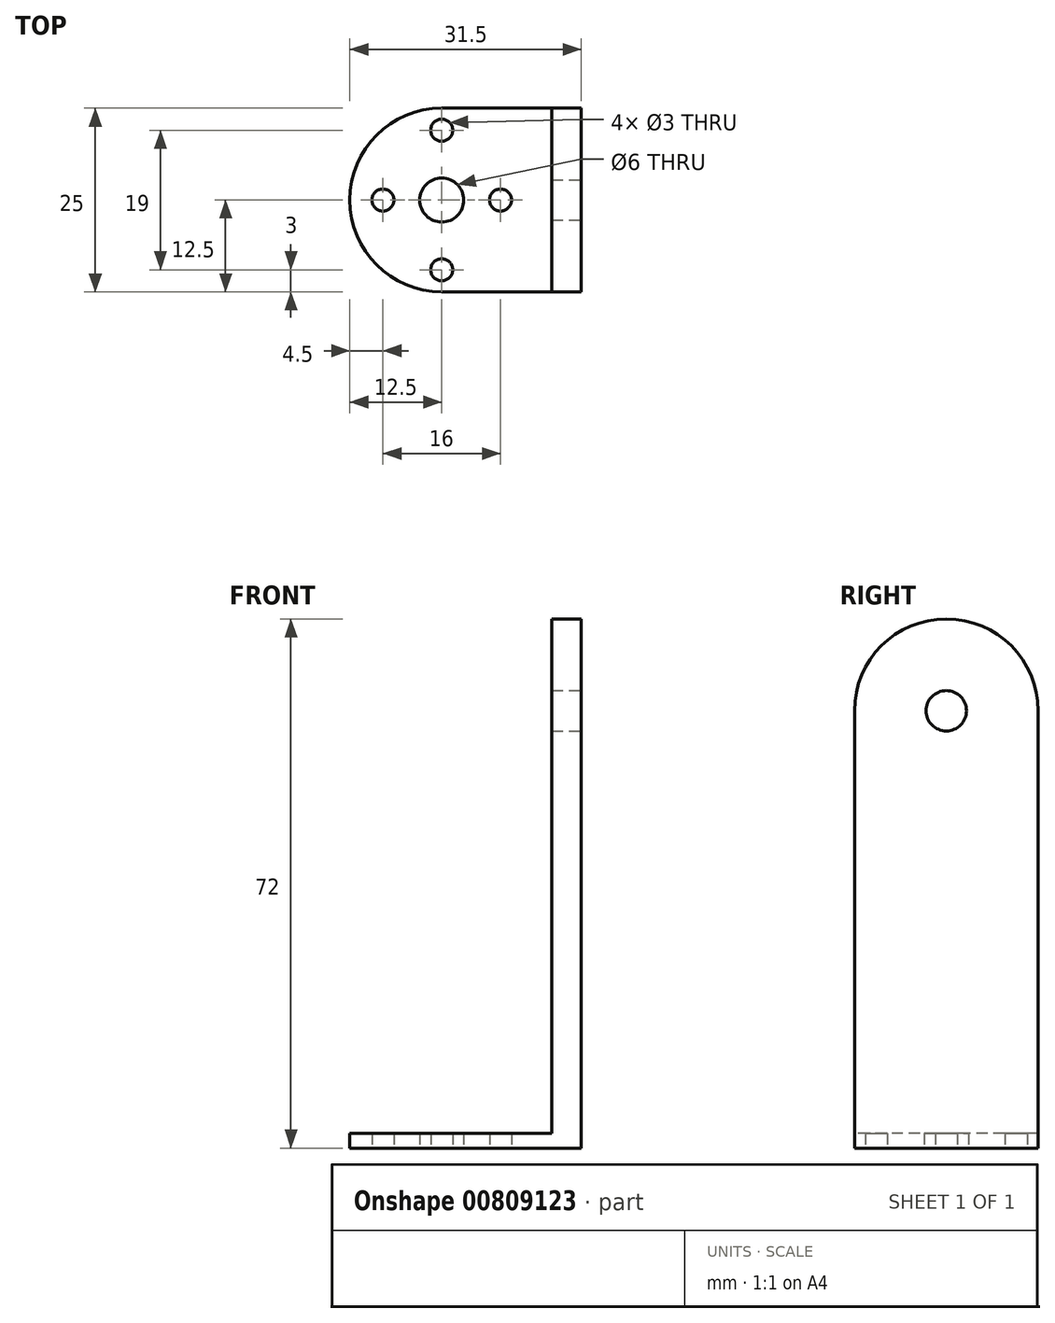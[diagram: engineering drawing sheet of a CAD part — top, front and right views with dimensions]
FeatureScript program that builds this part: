
annotation { "Feature Type Name" : "Feature", "Feature Type Description" : "" }
export const myFeature = defineFeature(function(context is Context, id is Id, definition is map)
    precondition{}
    {
        {
            var Q0;
            Q0=qCreatedBy(makeId("Top.planeOp"),FACE);
            var sketch = newSketch(context, id + "F0", { "sketchPlane" : qUnion([Q0])});
            skPoint(sketch, "E0.middle", {"position": v(0, 0) * mm});
            skCircle(sketch, "E1", {"center": v(0, 0) * mm, "radius": 9.5 * mm});
            skCircle(sketch, "E2", {"center": v(0, 0) * mm, "radius": 8 * mm});
            skCircle(sketch, "E3", {"center": v(0, -9.5) * mm, "radius": 1.5 * mm});
            skCircle(sketch, "E4", {"center": v(-8, 0) * mm, "radius": 1.5 * mm});
            skCircle(sketch, "E5", {"center": v(8, 0) * mm, "radius": 1.5 * mm});
            skCircle(sketch, "E6", {"center": v(0, 0) * mm, "radius": 12.5 * mm});
            skCircle(sketch, "E7", {"center": v(0, 0) * mm, "radius": 3 * mm});
            skCircle(sketch, "E8", {"center": v(0, 9.5) * mm, "radius": 1.5 * mm});
            skLineSegment(sketch, "E9", {"start": v(0, 12.5) * mm, "end": v(19, 12.5) * mm});
            skLineSegment(sketch, "E10", {"start": v(19, 12.5) * mm, "end": v(19, -12.5) * mm});
            skLineSegment(sketch, "E11", {"start": v(19, -12.5) * mm, "end": v(0, -12.5) * mm});
            skSolve(sketch);
        }
        {
            var Q0;
            Q0=makeQuery(id+"F0.imprint","IMPRINT",FACE,{"disambiguationData":[TD([[makeQuery(id+"F0.imprint","IMPRINT",EDGE,{"derivedFrom":sQuery(id+"F0.wireOp",EDGE,"E6")}),1.0]])]});
            var Q1;
            {var subQ0=sQuery(id+"F0.wireOp",EDGE,"PB5VHjtn-gHTu-7EB1-5jxL-tvkM96rimPre");var subQ1=sQuery(id+"F0.wireOp",EDGE,"E1");var subQ2=makeQuery(id+"F0.imprint","INTERSECT",VERTEX,{"disambiguationData":[OD(0.0)],"derivedFrom":[subQ1,subQ0]});Q1=makeQuery(id+"F0.imprint","IMPRINT",FACE,{"disambiguationData":[TD([[makeQuery(id+"F0.imprint","IMPRINT",EDGE,{"disambiguationData":[TD([[subQ2,1.0]])],"derivedFrom":subQ1}),1.0]])]});}
            var Q2;
            {var subQ0=sQuery(id+"F0.wireOp",EDGE,"PB5VHjtn-gHTu-7EB1-5jxL-tvkM96rimPre");var subQ1=sQuery(id+"F0.wireOp",EDGE,"E1");var subQ2=makeQuery(id+"F0.imprint","INTERSECT",VERTEX,{"disambiguationData":[OD(1.0)],"derivedFrom":[subQ1,subQ0]});Q2=makeQuery(id+"F0.imprint","IMPRINT",FACE,{"disambiguationData":[TD([[makeQuery(id+"F0.imprint","IMPRINT",EDGE,{"disambiguationData":[TD([[subQ2,-1.0]])],"derivedFrom":subQ1}),1.0]])]});}
            var Q3;
            {var subQ0=sQuery(id+"F0.wireOp",EDGE,"E4");var subQ1=sQuery(id+"F0.wireOp",EDGE,"E1");var subQ2=makeQuery(id+"F0.imprint","INTERSECT",VERTEX,{"derivedFrom":[subQ1,subQ0]});Q3=makeQuery(id+"F0.imprint","IMPRINT",FACE,{"disambiguationData":[TD([[makeQuery(id+"F0.imprint","IMPRINT",EDGE,{"disambiguationData":[TD([[subQ2,-1.0]])],"derivedFrom":subQ1}),1.0]])]});}
            var Q4;
            {var subQ0=sQuery(id+"F0.wireOp",EDGE,"E5");var subQ1=sQuery(id+"F0.wireOp",EDGE,"E1");var subQ2=makeQuery(id+"F0.imprint","INTERSECT",VERTEX,{"derivedFrom":[subQ1,subQ0]});Q4=makeQuery(id+"F0.imprint","IMPRINT",FACE,{"disambiguationData":[TD([[makeQuery(id+"F0.imprint","IMPRINT",EDGE,{"disambiguationData":[TD([[subQ2,1.0]])],"derivedFrom":subQ1}),1.0]])]});}
            var Q5;
            {var subQ0=sQuery(id+"F0.wireOp",EDGE,"E2");var subQ7=makeQuery(id+"F0.imprint","INTERSECT",VERTEX,{"derivedFrom":[subQ0,sQuery(id+"F0.wireOp",EDGE,"PB5VHjtn-gHTu-7EB1-5jxL-tvkM96rimPre")]});Q5=makeQuery(id+"F0.imprint","IMPRINT",FACE,{"disambiguationData":[TD([[makeQuery(id+"F0.imprint","IMPRINT",EDGE,{"disambiguationData":[TD([[subQ7,1.0]])],"derivedFrom":subQ0}),1.0]])]});}
            var Q6;
            {var subQ0=sQuery(id+"F0.wireOp",EDGE,"E8");var subQ1=sQuery(id+"F0.wireOp",EDGE,"E1");var subQ2=makeQuery(id+"F0.imprint","INTERSECT",VERTEX,{"disambiguationData":[OD(1.0)],"derivedFrom":[subQ1,subQ0]});Q6=makeQuery(id+"F0.imprint","IMPRINT",FACE,{"disambiguationData":[TD([[makeQuery(id+"F0.imprint","IMPRINT",EDGE,{"disambiguationData":[TD([[subQ2,-1.0]])],"derivedFrom":subQ1}),1.0]])]});}
            var Q7;
            {var subQ0=sQuery(id+"F0.wireOp",EDGE,"E8");var subQ1=sQuery(id+"F0.wireOp",EDGE,"E1");var subQ2=makeQuery(id+"F0.imprint","INTERSECT",VERTEX,{"disambiguationData":[OD(0.0)],"derivedFrom":[subQ1,subQ0]});Q7=makeQuery(id+"F0.imprint","IMPRINT",FACE,{"disambiguationData":[TD([[makeQuery(id+"F0.imprint","IMPRINT",EDGE,{"disambiguationData":[TD([[subQ2,1.0]])],"derivedFrom":subQ1}),1.0]])]});}
            var Q8;
            {var subQ0=sQuery(id+"F0.wireOp",EDGE,"E9");Q8=makeQuery(id+"F0.imprint","IMPRINT",FACE,{"disambiguationData":[TD([[makeQuery(id+"F0.imprint","IMPRINT",EDGE,{"derivedFrom":subQ0}),-1.0]])]});}
            extrude(context, id + "F1", {"entities" : qUnion([Q0, Q1, Q2, Q3, Q4, Q5, Q6, Q7, Q8]), "depth" : 2 * mm, "offsetDistance" : 25.4 * mm});
        }
        {
            var Q0;
            Q0=makeQuery(id+"F1.opExtrude","CAP_FACE",FACE,{"disambiguationData":[OSD([sQuery(id+"F0.wireOp",EDGE,"E3"),sQuery(id+"F0.wireOp",EDGE,"E4"),sQuery(id+"F0.wireOp",EDGE,"E5"),sQuery(id+"F0.wireOp",EDGE,"E6"),sQuery(id+"F0.wireOp",EDGE,"E7"),sQuery(id+"F0.wireOp",EDGE,"E8"),sQuery(id+"F0.wireOp",EDGE,"E9"),sQuery(id+"F0.wireOp",EDGE,"E10"),sQuery(id+"F0.wireOp",EDGE,"E11")])],"isStart":false});
            var sketch = newSketch(context, id + "F2", { "sketchPlane" : qUnion([Q0])});
            skLineSegment(sketch, "E12", {"start": v(15, 12.5) * mm, "end": v(15, -12.5) * mm});
            skSolve(sketch);
        }
        {
            var Q0;
            Q0 = qSketchRegion(id + "F2", true);
            var Q1;
            {var subQ0=sQuery(id+"F2.wireOp",EDGE,"E12");Q1=makeQuery(id+"F2.imprint","IMPRINT",FACE,{"disambiguationData":[TD([[makeQuery(id+"F2.imprint","IMPRINT",EDGE,{"derivedFrom":subQ0}),1.0]])]});}
            extrude(context, id + "F3", {"entities" : qUnion([Q0, Q1]), "operationType" : NewBodyOperationType.ADD, "depth" : 70 * mm, "offsetDistance" : 25.4 * mm});
        }
        {
            var Q0;
            {var subQ0=sQuery(id+"F0.wireOp",EDGE,"E10");Q0=makeQuery(id+"F3.boolean.opBoolean","MERGE",FACE,{"derivedFrom":[makeQuery(id+"F1.opExtrude","SWEPT_FACE",FACE,{"disambiguationData":[OSD([subQ0])]}),makeQuery(id+"F3.opExtrude","SWEPT_FACE",FACE,{"disambiguationData":[OSD([subQ0])]})]});}
            var sketch = newSketch(context, id + "F4", { "sketchPlane" : qUnion([Q0])});
            skCircle(sketch, "E13", {"center": v(0, 59.5) * mm, "radius": 2.75 * mm});
            skLineSegment(sketch, "E14", {"start": v(0, 59.5) * mm, "end": v(0, 72) * mm, "construction": true});
            skLineSegment(sketch, "E15", {"start": v(0, 59.5) * mm, "end": v(12.5, 59.5) * mm, "construction": true});
            skSolve(sketch);
        }
        {
            var Q0;
            Q0=makeQuery(id+"F4.imprint","IMPRINT",FACE,{"disambiguationData":[TD([[makeQuery(id+"F4.imprint","IMPRINT",EDGE,{"derivedFrom":sQuery(id+"F4.wireOp",EDGE,"E13")}),1.0]])]});
            extrude(context, id + "F5", {"entities" : qUnion([Q0]), "operationType" : NewBodyOperationType.REMOVE, "endBound" : BoundingType.THROUGH_ALL, "oppositeDirection" : true, "depth" : 25.4 * mm, "offsetDistance" : 25.4 * mm});
        }
        {
            var Q0;
            Q0=makeQuery(id+"F3.opExtrude","CAP_EDGE",EDGE,{"disambiguationData":[OSD([sQuery(id+"F0.wireOp",EDGE,"E11")])],"isStart":false});
            var Q1;
            Q1=makeQuery(id+"F3.opExtrude","CAP_EDGE",EDGE,{"disambiguationData":[OSD([sQuery(id+"F0.wireOp",EDGE,"E9")])],"isStart":false});
            fillet(context, id + "F6", {"entities" : qUnion([Q0, Q1]), "radius" : 12.5 * mm, "tangentPropagation" : true, "allowEdgeOverflow" : false});
        }
    });
